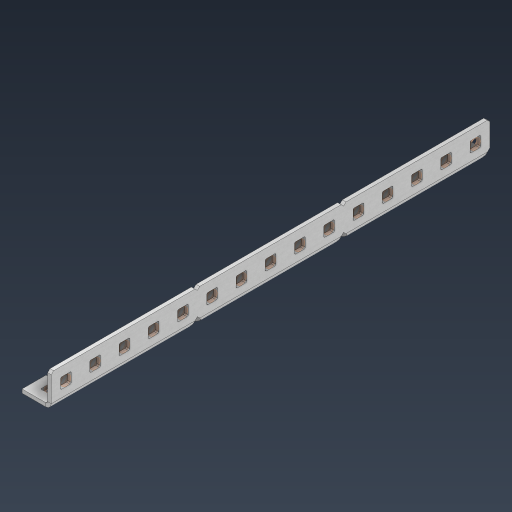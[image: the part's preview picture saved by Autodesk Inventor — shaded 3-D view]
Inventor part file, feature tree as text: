
AUTODESK INVENTOR PART (.ipt)
format: ipt  version: 2024.3 (Build 283343000, 343)  size: 736,768 bytes
history: native  units: in
note: dims shown in document units (in); Inventor stores cm internally (conversion verified against a paired STEP export)
features: other x52, extrude x43, sheet_metal_op x11, pattern_linear x2, mirror x1, chamfer x1, sketch x1
ambient origin geometry x8: Origin, YZ Plane, XZ Plane, XY Plane, X Axis, Y Axis, Z Axis, Center Point
bodies: Solid1 (feature_tree), Body (feature_tree)
feature tree (111):
  sheet_metal_op  "Flanges"
  other  "Flange Pattern Plane"
  other  "Flange Pattern Sketch"
  sheet_metal_op  "Flange Pattern"
  sheet_metal_op  "Body Pattern"
  pattern_linear  "Center Pattern"  Spacing1=7.5in  [1 undecoded]
  other  "Arc Length"
  mirror  "Notch Mirror"
  pattern_linear  "Notch Pattern"  Spacing1=0.0625in  [1 undecoded]
  chamfer  "End Chamfer"
  extrude  "Half Cut"  Depth=0.0625in
  other  "Plate1"
  sketch  "Sketch2"  dims[d0=1.0in d1=7.5in d2=0.0625in d3=0.0625in d4=0.0312in d5=0.125in d6=0.0625in d7=0.5in d8=90.0deg d9=0.0312in d10=0.25in d11=0.0625in d12=0.0625in d16=0.182in d17=0.02in d18=0.0625in d19=0.0in d20=0.25in d21=0.25in d38=5.9055in d40=0.5in d41=0.3937in d43=1.0in d46=0.172in d47=1.0in d48=0.0in d49=0.182in d50=0.02in d51=0.25in d52=0.25in d53=0.0625in d54=0.0in d55=0.172in d56=1.0in d57=0.0in d58=0.25in d60=5.9055in d62=0.5in d63=0.3937in d65=0.5in d85=0.1473in d86=0.1782in d88=0.04in d89=0.0625in d90=0.0in d91=0.04in d92=0.0491in d95=2.5in d96=0.04in d97=0.25in d98=45.0deg d99=0.25in d100=0.5in d101=0.0in d102=2.497in d106=0.182in d107=0.02in d108=0.5in d109=0.5in d110=0.0625in d111=0.0in d112=0.172in d113=0.5in d114=0.0in d117=0.5in d118=0.5in d119=0.5in]
  other  "Plate2"
  sheet_metal_op  "Bend1"
  sheet_metal_op  "Corner1"
  other  "Srf1"
  other  "Srf2"
  other  "Srf91"
  sheet_metal_op  "Body Pattern Sketch"
  other  "Srf92"
  other  "Srf786"
  other  "Srf823"
  other  "Srf824"
  other  "Srf825"
  other  "Srf826"
  other  "Srf827"
  other  "Srf828"
  other  "Srf829"
  other  "Srf856"
  other  "Srf857"
  other  "Srf858"
  other  "Srf859"
  other  "Srf860"
  other  "Srf861"
  other  "Srf862"
  other  "Srf889"
  other  "Srf890"
  other  "Srf891"
  other  "Srf892"
  other  "Srf893"
  other  "Srf894"
  other  "Srf895"
  other  "Srf896"
  other  "Srf922"
  other  "Srf923"
  other  "Srf924"
  other  "Srf925"
  other  "Srf926"
  other  "Srf959"
  other  "Srf960"
  other  "Srf961"
  other  "Srf962"
  other  "Srf963"
  other  "Srf996"
  other  "Srf997"
  other  "Srf998"
  other  "Srf999"
  other  "Srf1000"
  other  "Srf1143"
  other  "Srf1199"
  other  "Srf1255"
  sheet_metal_op  "Flange Stamp"
  sheet_metal_op  "Flange Circle"
  sheet_metal_op  "Body Stamp"
  sheet_metal_op  "Body Circle"
  other  "Center Stamp"
  other  "Center Circle"
  sheet_metal_op  "Notch"
  extrude  "ExtrusionSrf2"  Depth=0.0312in
  extrude  "ExtrusionSrf92"  Depth=0.5in
  extrude  "ExtrusionSrf823"  Depth=0.0625in
  extrude  "ExtrusionSrf824"  Depth=0.5in TaperAngle=90.0deg
  extrude  "ExtrusionSrf825"  Depth=0.5in
  extrude  "ExtrusionSrf826"  Depth=0.0625in
  extrude  "ExtrusionSrf827"  Depth=0.0625in
  extrude  "ExtrusionSrf828"  Depth=0.182in
  extrude  "ExtrusionSrf829"  Depth=0.02in
  extrude  "ExtrusionSrf856"  Depth=0.0625in
  extrude  "ExtrusionSrf857"  TaperAngle=0.0deg  [1 undecoded]
  extrude  "ExtrusionSrf858"  Depth=0.5in
  extrude  "ExtrusionSrf859"  Depth=0.5in
  extrude  "ExtrusionSrf860"  Depth=0.5in
  extrude  "ExtrusionSrf861"  Depth=0.5in
  extrude  "ExtrusionSrf862"  Depth=1.0in TaperAngle=0.0deg
  extrude  "ExtrusionSrf889"  Depth=0.182in
  extrude  "ExtrusionSrf890"  Depth=0.02in
  extrude  "ExtrusionSrf891"  Depth=0.5in
  extrude  "ExtrusionSrf892"  Depth=0.5in
  extrude  "ExtrusionSrf893"  Depth=0.0625in
  extrude  "ExtrusionSrf894"  TaperAngle=0.0deg  [1 undecoded]
  extrude  "ExtrusionSrf895"  Depth=0.5in
  extrude  "ExtrusionSrf896"  Depth=1.0in TaperAngle=0.0deg
  extrude  "ExtrusionSrf922"  Depth=0.5in
  extrude  "ExtrusionSrf923"  Depth=0.5in
  extrude  "ExtrusionSrf924"  Depth=0.5in
  extrude  "ExtrusionSrf925"  Depth=0.5in
  extrude  "ExtrusionSrf926"  Depth=0.5in
  extrude  "ExtrusionSrf959"  Depth=0.5in
  extrude  "ExtrusionSrf960"  Depth=0.0625in
  extrude  "ExtrusionSrf961"  TaperAngle=0.0deg  [1 undecoded]
  extrude  "ExtrusionSrf962"  Depth=0.5in
  extrude  "ExtrusionSrf963"  Depth=0.5in
  extrude  "ExtrusionSrf996"  Depth=2.5in
  extrude  "ExtrusionSrf997"  Depth=0.5in TaperAngle=45.0deg
  extrude  "ExtrusionSrf998"  Depth=0.5in
  extrude  "ExtrusionSrf999"  Depth=0.5in TaperAngle=0.0deg
  extrude  "ExtrusionSrf1000"  Depth=0.5in
  extrude  "ExtrusionSrf1143"  Depth=0.182in
  extrude  "ExtrusionSrf1199"  Depth=0.02in
  extrude  "ExtrusionSrf1255"  Depth=0.5in
note: 5 required parameter values undecoded (feature->parameter linkage not recoverable at this tier; creation-order binding heuristic only, values carry confidence <= 0.55)
